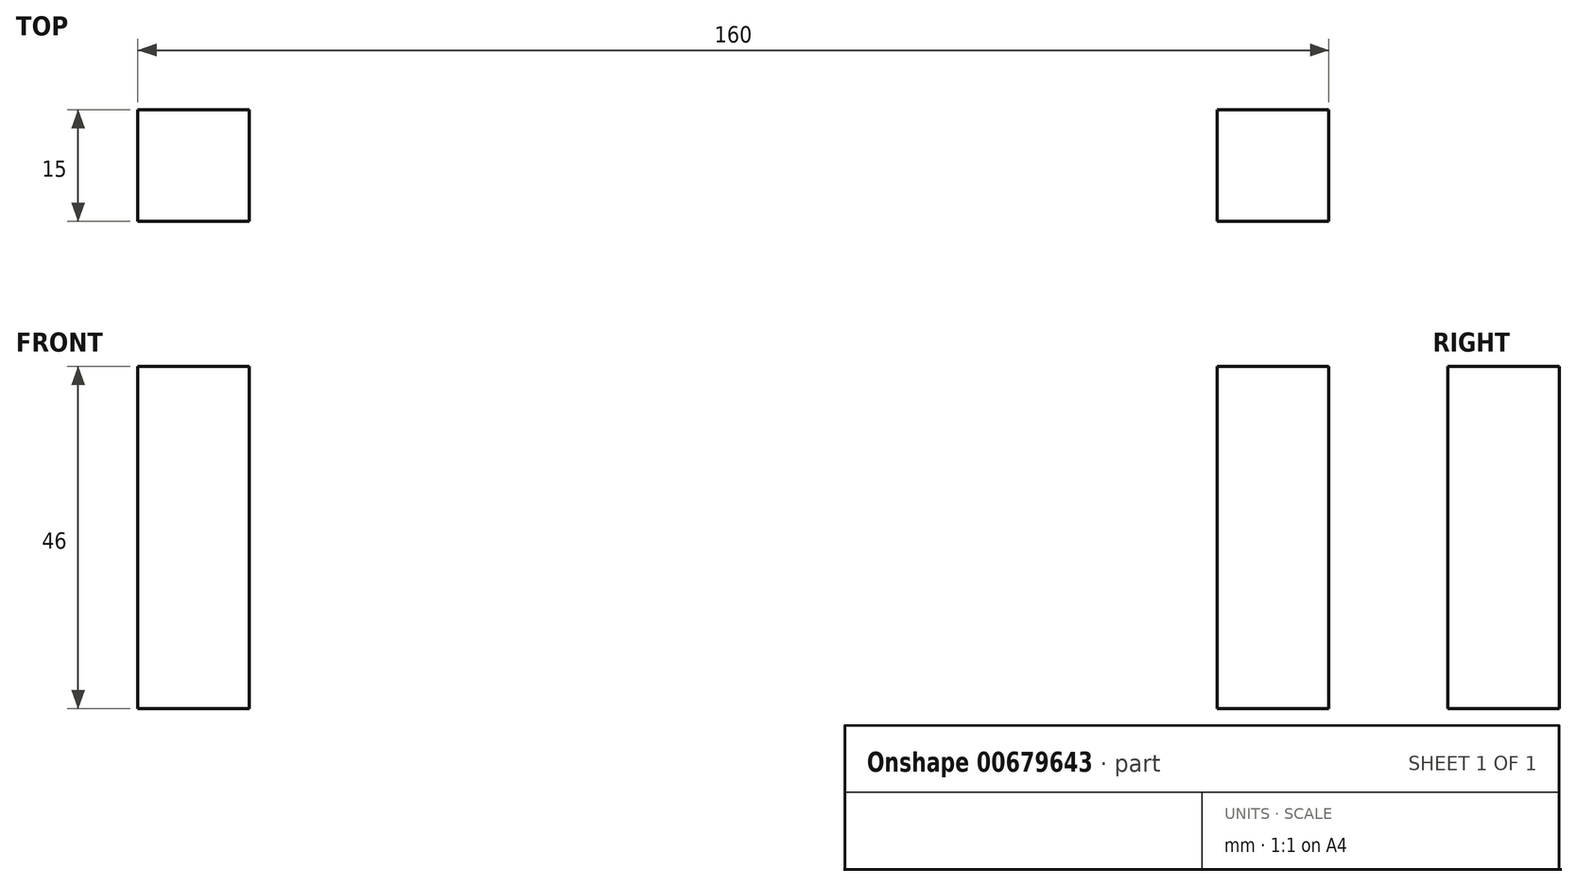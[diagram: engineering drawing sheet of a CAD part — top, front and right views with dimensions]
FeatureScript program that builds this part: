
annotation { "Feature Type Name" : "Feature", "Feature Type Description" : "" }
export const myFeature = defineFeature(function(context is Context, id is Id, definition is map)
    precondition{}
    {
        {
            var Q0;
            Q0=qCreatedBy(makeId("Front.planeOp"),FACE);
            var sketch = newSketch(context, id + "F0", { "sketchPlane" : qUnion([Q0])});
            skLineSegment(sketch, "E0.bottom", {"start": v(-100, 10) * mm, "end": v(100, 10) * mm});
            skLineSegment(sketch, "E0.top", {"start": v(-100, -10) * mm, "end": v(100, -10) * mm});
            skLineSegment(sketch, "E0.left", {"start": v(-100, 10) * mm, "end": v(-100, -10) * mm});
            skLineSegment(sketch, "E0.right", {"start": v(100, 10) * mm, "end": v(100, -10) * mm});
            skPoint(sketch, "E0.middle", {"position": v(0, 0) * mm});
            skCircle(sketch, "E1", {"center": v(0, 33) * mm, "radius": 28 * mm});
            skPoint(sketch, "E1.centerSnap1", {"position": v(0, 10) * mm});
            skCircle(sketch, "E2", {"center": v(0, 33) * mm, "radius": 23 * mm});
            skLineSegment(sketch, "E3.bottom", {"start": v(65, 56) * mm, "end": v(80, 56) * mm});
            skLineSegment(sketch, "E3.top", {"start": v(65, 0) * mm, "end": v(80, 0) * mm});
            skLineSegment(sketch, "E3.left", {"start": v(65, 56) * mm, "end": v(65, 0) * mm});
            skLineSegment(sketch, "E3.right", {"start": v(80, 56) * mm, "end": v(80, 0) * mm});
            skPoint(sketch, "E4", {"position": v(-100, 0) * mm});
            skLineSegment(sketch, "E5.bottom", {"start": v(-80, 56) * mm, "end": v(-65, 56) * mm});
            skLineSegment(sketch, "E5.top", {"start": v(-80, 0) * mm, "end": v(-65, 0) * mm});
            skLineSegment(sketch, "E5.left", {"start": v(-80, 56) * mm, "end": v(-80, 0) * mm});
            skLineSegment(sketch, "E5.right", {"start": v(-65, 56) * mm, "end": v(-65, 0) * mm});
            skSolve(sketch);
        }
        {
            var Q0;
            {var subQ5=sQuery(id+"F0.wireOp",EDGE,"E5.bottom");Q0=makeQuery(id+"F0.imprint","IMPRINT",FACE,{"disambiguationData":[TD([[makeQuery(id+"F0.imprint","IMPRINT",EDGE,{"derivedFrom":subQ5}),-1.0]])]});}
            var Q1;
            {var subQ5=sQuery(id+"F0.wireOp",EDGE,"E3.bottom");Q1=makeQuery(id+"F0.imprint","IMPRINT",FACE,{"disambiguationData":[TD([[makeQuery(id+"F0.imprint","IMPRINT",EDGE,{"derivedFrom":subQ5}),-1.0]])]});}
            extrude(context, id + "F1", {"entities" : qUnion([Q0, Q1]), "depth" : 15 * mm, "offsetDistance" : 25 * mm});
        }
    });
